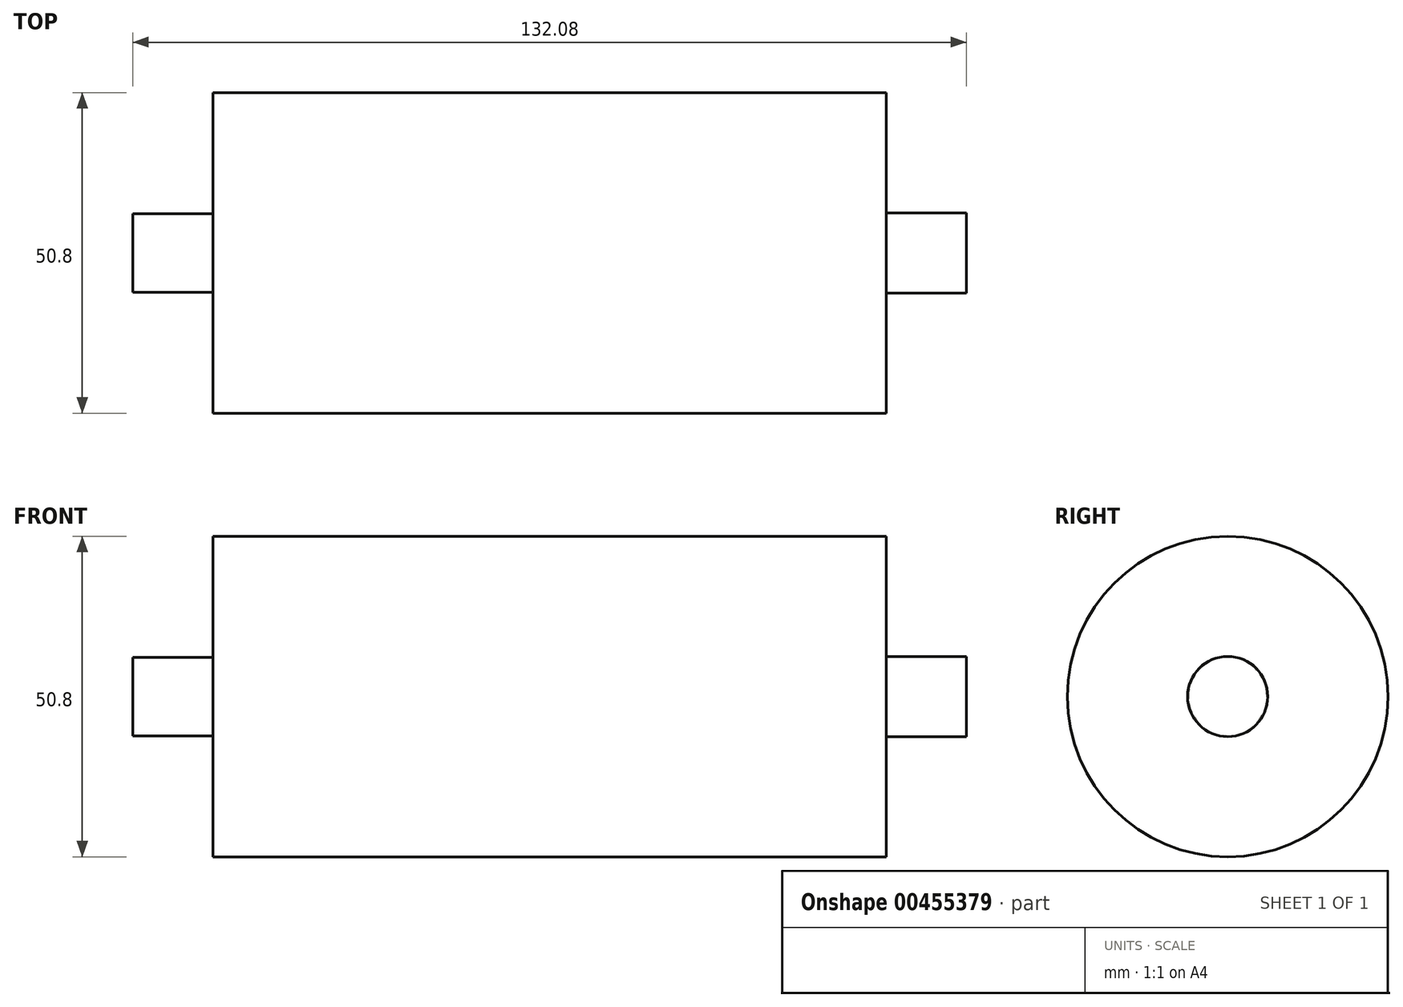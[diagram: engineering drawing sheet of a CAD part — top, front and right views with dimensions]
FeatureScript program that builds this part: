
annotation { "Feature Type Name" : "Feature", "Feature Type Description" : "" }
export const myFeature = defineFeature(function(context is Context, id is Id, definition is map)
    precondition{}
    {
        {
            var Q0;
            Q0=qCreatedBy(makeId("Top.planeOp"),FACE);
            var sketch = newSketch(context, id + "F0", { "sketchPlane" : qUnion([Q0])});
            skLineSegment(sketch, "E0.bottom", {"start": v(-53.65, -10.81) * mm, "end": v(53.03, -10.81) * mm});
            skLineSegment(sketch, "E0.top", {"start": v(-53.65, -36.21) * mm, "end": v(53.03, -36.21) * mm});
            skLineSegment(sketch, "E0.left", {"start": v(-53.65, -10.81) * mm, "end": v(-53.65, -36.21) * mm});
            skLineSegment(sketch, "E0.right", {"start": v(53.03, -10.81) * mm, "end": v(53.03, -36.21) * mm});
            skSolve(sketch);
        }
        {
            var Q0;
            Q0=makeQuery(id+"F0.imprint","IMPRINT",FACE,{"disambiguationData":[TD([[makeQuery(id+"F0.imprint","IMPRINT",EDGE,{"derivedFrom":sQuery(id+"F0.wireOp",EDGE,"E0.bottom")}),-1.0]])]});
            var Q1;
            Q1=sQuery(id+"F0.wireOp",EDGE,"E0.bottom");
            revolve(context, id + "F1", {"entities" : qUnion([Q0]), "axis" : qUnion([Q1]), "revolveType" : RevolveType.FULL});
        }
        {
            var Q0;
            Q0=makeQuery(id+"F1.opRevolve","SWEPT_FACE",FACE,{"disambiguationData":[OSD([sQuery(id+"F0.wireOp",EDGE,"E0.left")])]});
            var sketch = newSketch(context, id + "F2", { "sketchPlane" : qUnion([Q0])});
            skCircle(sketch, "E1", {"center": v(10.81, 0) * mm, "radius": 6.22 * mm});
            skSolve(sketch);
        }
        {
            var Q0;
            Q0=makeQuery(id+"F2.imprint","IMPRINT",FACE,{"disambiguationData":[TD([[makeQuery(id+"F2.imprint","IMPRINT",EDGE,{"derivedFrom":sQuery(id+"F2.wireOp",EDGE,"E1")}),1.0]])]});
            extrude(context, id + "F3", {"entities" : qUnion([Q0]), "operationType" : NewBodyOperationType.ADD, "depth" : 12.7 * mm});
        }
        {
            var Q0;
            Q0=makeQuery(id+"F1.opRevolve","SWEPT_FACE",FACE,{"disambiguationData":[OSD([sQuery(id+"F0.wireOp",EDGE,"E0.right")])]});
            var sketch = newSketch(context, id + "F4", { "sketchPlane" : qUnion([Q0])});
            skCircle(sketch, "E2", {"center": v(-10.81, 0) * mm, "radius": 6.35 * mm});
            skSolve(sketch);
        }
        {
            var Q0;
            Q0=makeQuery(id+"F4.imprint","IMPRINT",FACE,{"disambiguationData":[TD([[makeQuery(id+"F4.imprint","IMPRINT",EDGE,{"derivedFrom":sQuery(id+"F4.wireOp",EDGE,"E2")}),1.0]])]});
            extrude(context, id + "F5", {"entities" : qUnion([Q0]), "operationType" : NewBodyOperationType.ADD, "depth" : 12.7 * mm});
        }
    });
